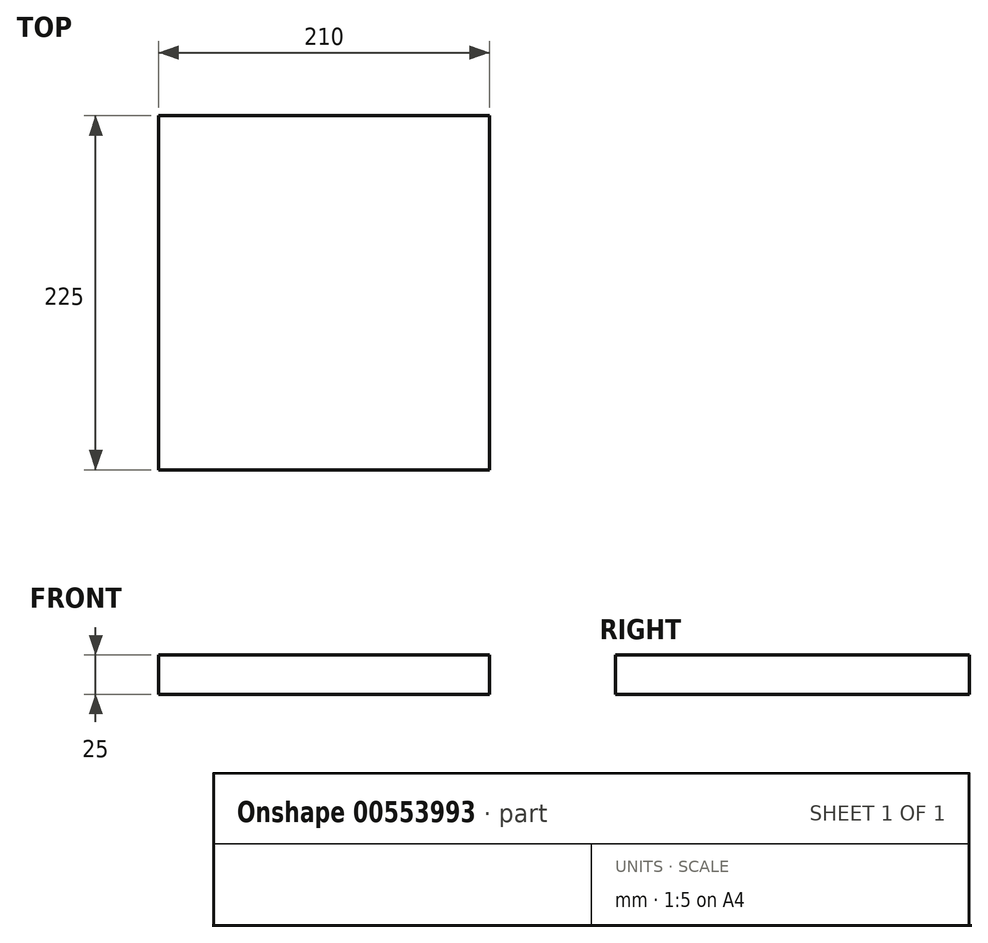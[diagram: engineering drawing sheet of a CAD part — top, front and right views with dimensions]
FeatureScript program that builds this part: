
annotation { "Feature Type Name" : "Feature", "Feature Type Description" : "" }
export const myFeature = defineFeature(function(context is Context, id is Id, definition is map)
    precondition{}
    {
        {
            var Q0;
            Q0=qCreatedBy(makeId("Top.planeOp"),FACE);
            var sketch = newSketch(context, id + "F0", { "sketchPlane" : qUnion([Q0])});
            skLineSegment(sketch, "E0.bottom", {"start": v(105, 112.5) * mm, "end": v(-105, 112.5) * mm});
            skLineSegment(sketch, "E0.top", {"start": v(105, -112.5) * mm, "end": v(-105, -112.5) * mm});
            skLineSegment(sketch, "E0.left", {"start": v(105, 112.5) * mm, "end": v(105, -112.5) * mm});
            skLineSegment(sketch, "E0.right", {"start": v(-105, 112.5) * mm, "end": v(-105, -112.5) * mm});
            skPoint(sketch, "E0.middle", {"position": v(0, 0) * mm});
            skSolve(sketch);
        }
        {
            var Q0;
            Q0=makeQuery(id+"F0.imprint","IMPRINT",FACE,{"disambiguationData":[TD([[makeQuery(id+"F0.imprint","IMPRINT",EDGE,{"derivedFrom":sQuery(id+"F0.wireOp",EDGE,"E0.bottom")}),1.0]])]});
            extrude(context, id + "F1", {"entities" : qUnion([Q0]), "depth" : 25 * mm, "offsetDistance" : 25 * mm});
        }
    });
